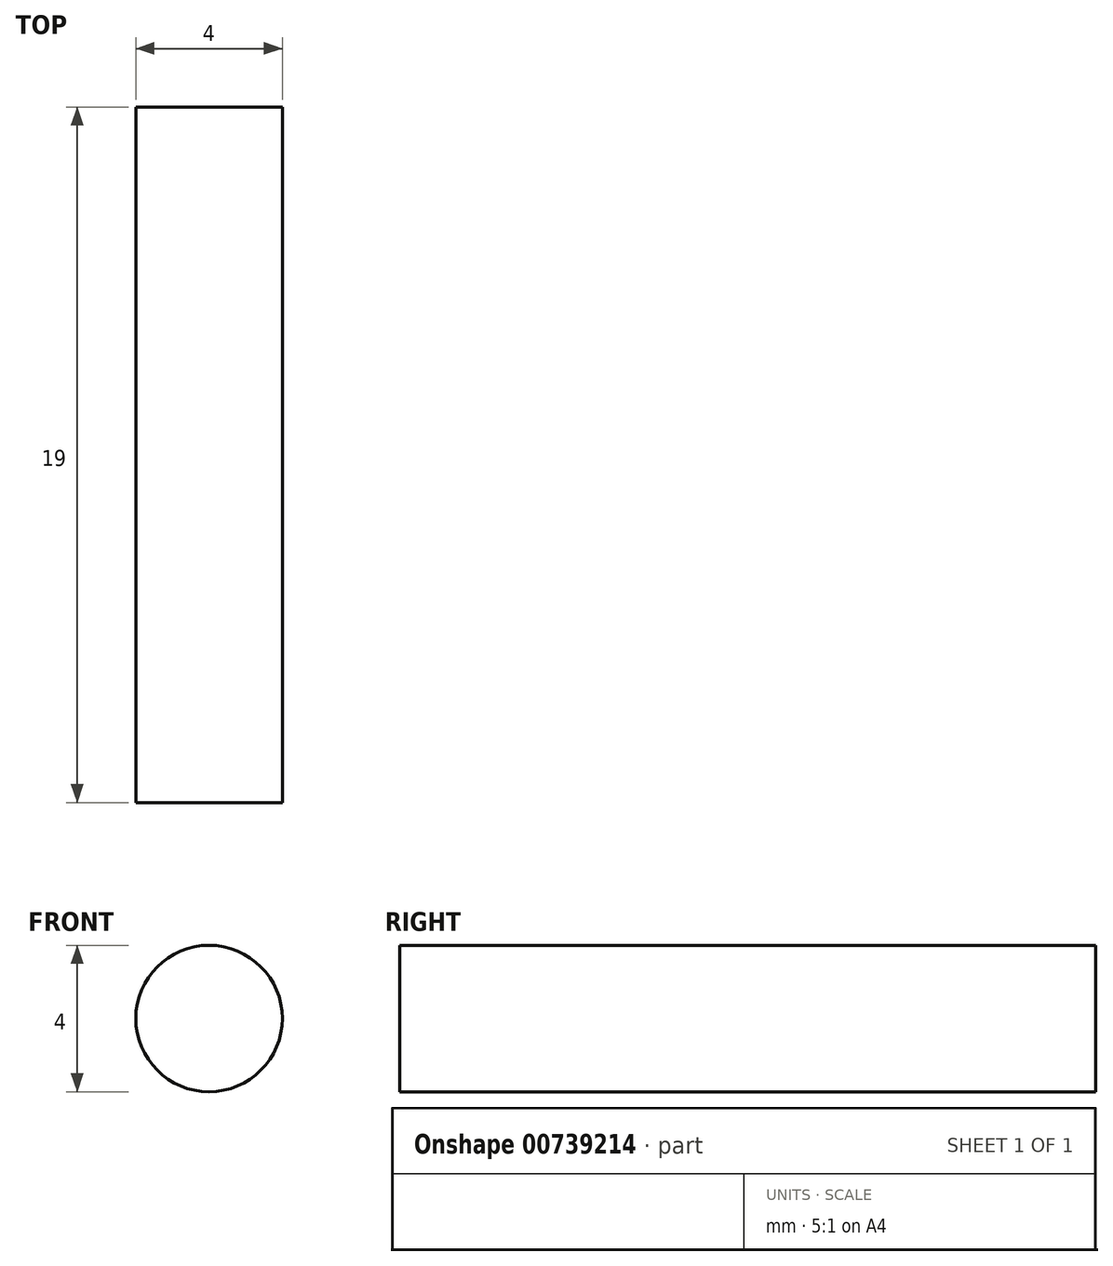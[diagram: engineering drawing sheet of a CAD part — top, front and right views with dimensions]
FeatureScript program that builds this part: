
annotation { "Feature Type Name" : "Feature", "Feature Type Description" : "" }
export const myFeature = defineFeature(function(context is Context, id is Id, definition is map)
    precondition{}
    {
        {
            var Q0;
            Q0=qCreatedBy(makeId("Front.planeOp"),FACE);
            var sketch = newSketch(context, id + "F0", { "sketchPlane" : qUnion([Q0])});
            skCircle(sketch, "E0", {"center": v(0, 0) * mm, "radius": 2 * mm});
            skSolve(sketch);
        }
        {
            var Q0;
            Q0 = qSketchRegion(id + "F0", true);
            extrude(context, id + "F1", {"entities" : qUnion([Q0]), "depth" : 19 * mm, "offsetDistance" : 25.4 * mm});
        }
    });
